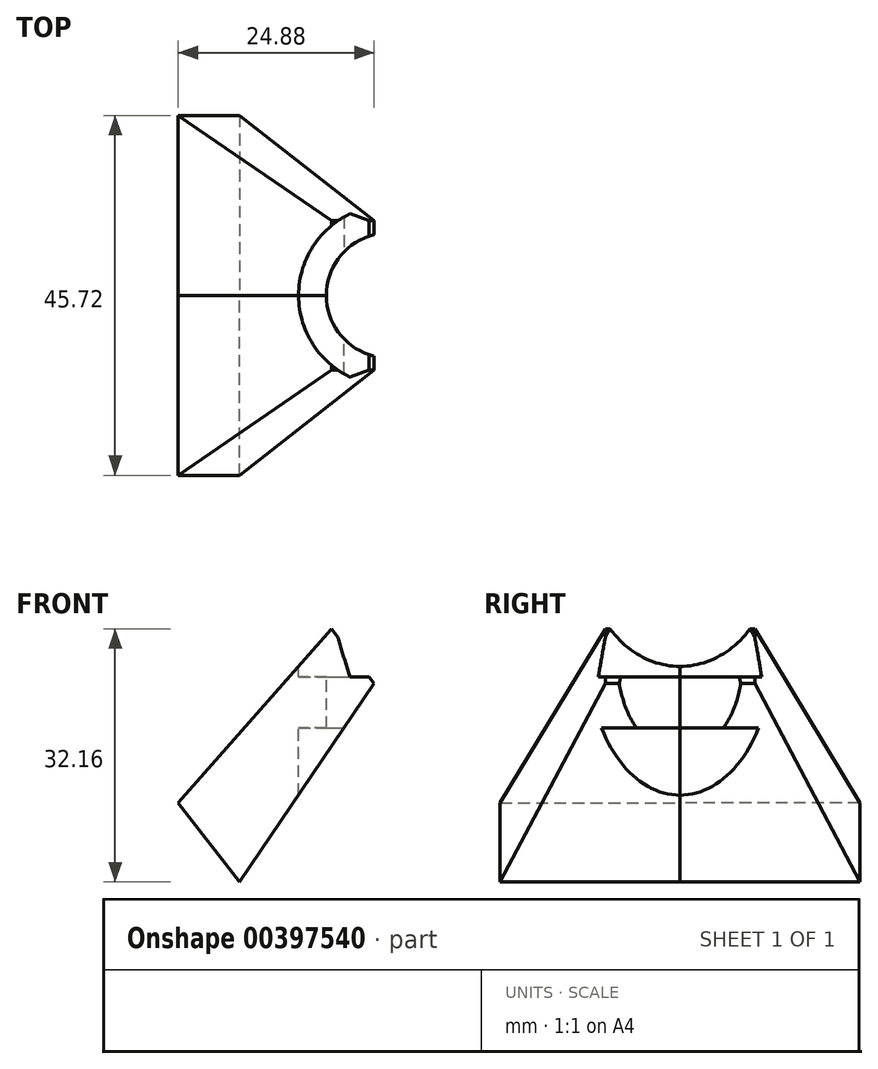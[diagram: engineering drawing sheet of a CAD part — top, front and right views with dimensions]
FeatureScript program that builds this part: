
annotation { "Feature Type Name" : "Feature", "Feature Type Description" : "" }
export const myFeature = defineFeature(function(context is Context, id is Id, definition is map)
    precondition{}
    {
        {
            var Q0;
            Q0=qCreatedBy(makeId("Front.planeOp"),FACE);
            var sketch = newSketch(context, id + "F0", { "sketchPlane" : qUnion([Q0])});
            skLineSegment(sketch, "E0.bottom", {"start": v(-14.27, 4.76) * mm, "end": v(-11.48, 4.76) * mm});
            skLineSegment(sketch, "E0.top", {"start": v(-14.27, -4.76) * mm, "end": v(-11.48, -4.76) * mm});
            skLineSegment(sketch, "E0.left", {"start": v(-14.27, 4.76) * mm, "end": v(-14.27, -4.76) * mm});
            skLineSegment(sketch, "E0.right", {"start": v(-11.48, 4.76) * mm, "end": v(-11.48, 3.24) * mm});
            skLineSegment(sketch, "E1.bottom", {"start": v(-11.48, 3.24) * mm, "end": v(-7.94, 3.24) * mm});
            skLineSegment(sketch, "E1.top", {"start": v(-11.48, -3.24) * mm, "end": v(-7.94, -3.24) * mm});
            skLineSegment(sketch, "E1.right", {"start": v(-7.94, 3.24) * mm, "end": v(-7.94, -3.24) * mm});
            skLineSegment(sketch, "E2", {"start": v(-7.94, 0) * mm, "end": v(0, 0) * mm, "construction": true});
            skLineSegment(sketch, "E3.trimOffspring", {"start": v(-11.48, -3.24) * mm, "end": v(-11.48, -4.76) * mm});
            skLineSegment(sketch, "E4", {"start": v(0, 0) * mm, "end": v(0, 7.19) * mm, "construction": true});
            skSolve(sketch);
        }
        {
            var Q0;
            Q0 = qConstructionFilter(qBodyType(qCreatedBy(id + "F0" ,EDGE), BodyType.WIRE), ConstructionObject.NO);
            var Q1;
            Q1=sQuery(id+"F0.wireOp",EDGE,"E4");
            revolve(context, id + "F1", {"bodyType" : ToolBodyType.SURFACE, "surfaceEntities" : qUnion([Q0]), "axis" : qUnion([Q1]), "revolveType" : RevolveType.FULL});
        }
        {
            var Q0;
            Q0=qCreatedBy(makeId("Top.planeOp"),FACE);
            cPlane(context, id + "F2", {"entities" : qUnion([Q0]), "cplaneType" : CPlaneType.OFFSET, "offset" : 17.78 * mm, "oppositeDirection" : true, "width" : 152.4 * mm, "height" : 152.4 * mm});
        }
        {
            var Q0;
            Q0=qCreatedBy(id+"F2.planeOp",FACE);
            var sketch = newSketch(context, id + "F3", { "sketchPlane" : qUnion([Q0])});
            skLineSegment(sketch, "E5", {"start": v(-22.86, 0) * mm, "end": v(-22.86, -54.6) * mm});
            skLineSegment(sketch, "E6", {"start": v(-22.86, 0) * mm, "end": v(-29.21, 0) * mm});
            skLineSegment(sketch, "E7", {"start": v(-29.21, 0) * mm, "end": v(-29.2, -25.4) * mm});
            skLineSegment(sketch, "E8", {"start": v(-29.2, -25.4) * mm, "end": v(-30.48, -25.4) * mm});
            skLineSegment(sketch, "E9", {"start": v(-30.48, -25.4) * mm, "end": v(-30.48, -29.21) * mm});
            skLineSegment(sketch, "E10", {"start": v(-30.48, -29.21) * mm, "end": v(-26.04, -29.21) * mm});
            skLineSegment(sketch, "E11", {"start": v(-26.04, -29.21) * mm, "end": v(-26.03, -54.6) * mm});
            skLineSegment(sketch, "E12", {"start": v(-26.03, -54.61) * mm, "end": v(-22.86, -54.61) * mm});
            skSolve(sketch);
        }
        {
            var Q0;
            Q0=sQuery(id+"F3.wireOp",EDGE,"E6");
            var Q1;
            Q1=sQuery(id+"F3.wireOp",EDGE,"E7");
            var Q2;
            Q2=sQuery(id+"F3.wireOp",EDGE,"E8");
            var Q3;
            Q3=sQuery(id+"F3.wireOp",EDGE,"E9");
            var Q4;
            Q4=sQuery(id+"F3.wireOp",EDGE,"E10");
            var Q5;
            Q5=sQuery(id+"F3.wireOp",EDGE,"E11");
            var Q6;
            Q6=sQuery(id+"F3.wireOp",EDGE,"E12");
            var Q7;
            Q7=sQuery(id+"F3.wireOp",EDGE,"E5");
            revolve(context, id + "F4", {"bodyType" : ToolBodyType.SURFACE, "surfaceEntities" : qUnion([Q0, Q1, Q2, Q3, Q4, Q5, Q6]), "axis" : qUnion([Q7]), "revolveType" : RevolveType.FULL});
        }
        {
            var Q0;
            Q0=qCreatedBy(makeId("Front.planeOp"),FACE);
            var sketch = newSketch(context, id + "F5", { "sketchPlane" : qUnion([Q0])});
            skLineSegment(sketch, "E13", {"start": v(0, 0) * mm, "end": v(-22.86, -17.78) * mm});
            skSolve(sketch);
        }
        {
            var Q0;
            Q0=sQuery(id+"F5.wireOp",EDGE,"E13");
            var Q1;
            Q1=sQuery(id+"F5.wireOp",VERTEX,"E13.end");
            cPlane(context, id + "F6", {"entities" : qUnion([Q0, Q1]), "cplaneType" : CPlaneType.LINE_POINT, "offset" : 25.4 * mm, "width" : 152.4 * mm, "height" : 152.4 * mm});
        }
        {
            var Q0;
            Q0=qCreatedBy(id+"F6.planeOp",FACE);
            var sketch = newSketch(context, id + "F7", { "sketchPlane" : qUnion([Q0])});
            skLineSegment(sketch, "E14.bottom", {"start": v(22.86, -6.35) * mm, "end": v(0, -6.35) * mm});
            skLineSegment(sketch, "E14.top", {"start": v(22.86, 6.35) * mm, "end": v(0, 6.35) * mm});
            skLineSegment(sketch, "E14.left", {"start": v(22.86, -6.35) * mm, "end": v(22.86, 6.35) * mm});
            skLineSegment(sketch, "E14.right", {"start": v(0, -6.35) * mm, "end": v(0, 6.35) * mm});
            skSolve(sketch);
        }
        {
            var Q0;
            Q0=sQuery(id+"F5.wireOp",EDGE,"E13");
            var Q1;
            Q1=sQuery(id+"F5.wireOp",VERTEX,"E13.start");
            cPlane(context, id + "F8", {"entities" : qUnion([Q0, Q1]), "cplaneType" : CPlaneType.LINE_POINT, "offset" : 25.4 * mm, "width" : 152.4 * mm, "height" : 152.4 * mm});
        }
        {
            var Q0;
            Q0=qCreatedBy(id+"F8.planeOp",FACE);
            var sketch = newSketch(context, id + "F9", { "sketchPlane" : qUnion([Q0])});
            skLineSegment(sketch, "E15.bottom", {"start": v(0, 3.06) * mm, "end": v(9.5, 3.06) * mm});
            skLineSegment(sketch, "E15.top", {"start": v(0, 11.87) * mm, "end": v(9.5, 11.87) * mm});
            skLineSegment(sketch, "E15.left", {"start": v(0, 3.06) * mm, "end": v(0, 11.87) * mm});
            skLineSegment(sketch, "E15.right", {"start": v(9.5, 3.06) * mm, "end": v(9.5, 11.87) * mm});
            skSolve(sketch);
        }
        {
            var Q0;
            Q0 = qSketchRegion(id + "F7", true);
            var Q1;
            Q1 = qSketchRegion(id + "F9", true);
            loft(context, id + "F10", {"sheetProfilesArray" : [{ "sheetProfileEntities" : qUnion([Q0]) }, { "sheetProfileEntities" : qUnion([Q1]) }]});
        }
        {
            var Q0;
            Q0=qCreatedBy(makeId("Front.planeOp"),FACE);
            var sketch = newSketch(context, id + "F11", { "sketchPlane" : qUnion([Q0])});
            skLineSegment(sketch, "E16.0", {"start": v(-11.48, 4.76) * mm, "end": v(-11.48, 3.24) * mm});
            skLineSegment(sketch, "E16.1", {"start": v(-11.48, 3.24) * mm, "end": v(-7.94, 3.24) * mm});
            skLineSegment(sketch, "E16.2", {"start": v(-7.94, 3.24) * mm, "end": v(-7.94, -3.24) * mm});
            skLineSegment(sketch, "E16.3", {"start": v(-11.48, -3.24) * mm, "end": v(-7.94, -3.24) * mm});
            skLineSegment(sketch, "E16.4", {"start": v(-11.48, -3.24) * mm, "end": v(-11.48, -4.76) * mm});
            skLineSegment(sketch, "E17", {"start": v(-11.48, 4.76) * mm, "end": v(-11.48, 13.3) * mm});
            skLineSegment(sketch, "E18", {"start": v(0, 13.3) * mm, "end": v(0, 13.3) * mm});
            skLineSegment(sketch, "E19", {"start": v(0, 13.3) * mm, "end": v(-11.48, 13.3) * mm});
            skLineSegment(sketch, "E20", {"start": v(0, 13.3) * mm, "end": v(0, 0) * mm});
            skLineSegment(sketch, "E21", {"start": v(-11.48, -4.76) * mm, "end": v(-11.48, -25.4) * mm});
            skLineSegment(sketch, "E22", {"start": v(-11.48, -25.4) * mm, "end": v(0, -25.4) * mm});
            skLineSegment(sketch, "E23", {"start": v(0, -25.4) * mm, "end": v(0, 0) * mm});
            skSolve(sketch);
        }
        {
            var Q0;
            Q0=makeQuery(id+"F11.imprint","IMPRINT",FACE,{"disambiguationData":[TD([[makeQuery(id+"F11.imprint","IMPRINT",EDGE,{"derivedFrom":sQuery(id+"F11.wireOp",EDGE,"E16.0")}),1.0]])]});
            var Q1;
            Q1=sQuery(id+"F11.wireOp",EDGE,"E23");
            revolve(context, id + "F12", {"operationType" : NewBodyOperationType.REMOVE, "entities" : qUnion([Q0]), "axis" : qUnion([Q1]), "revolveType" : RevolveType.FULL, "oppositeDirection" : true});
        }
        {
            var Q0;
            Q0=makeQuery(id+"F4.opRevolve","SWEPT_BODY",BODY,{"disambiguationData":[OSD([sQuery(id+"F3.wireOp",EDGE,"E12")])]});
            var Q1;
            Q1=makeQuery(id+"F10.opLoft","SWEPT_BODY",BODY,{"disambiguationData":[OSD([makeQuery(id+"F7.imprint","IMPRINT",FACE,{"disambiguationData":[TD([[makeQuery(id+"F7.imprint","IMPRINT",EDGE,{"derivedFrom":sQuery(id+"F7.wireOp",EDGE,"E14.bottom")}),-1.0]])]}),makeQuery(id+"F9.imprint","IMPRINT",FACE,{"disambiguationData":[TD([[makeQuery(id+"F9.imprint","IMPRINT",EDGE,{"derivedFrom":sQuery(id+"F9.wireOp",EDGE,"E15.bottom")}),1.0]])]})])]});
            var Q2;
            Q2=qCreatedBy(makeId("Front.planeOp"),FACE);
            mirror(context, id + "F13", {"entities" : qUnion([Q0, Q1]), "mirrorPlane" : qUnion([Q2])});
        }
    });
